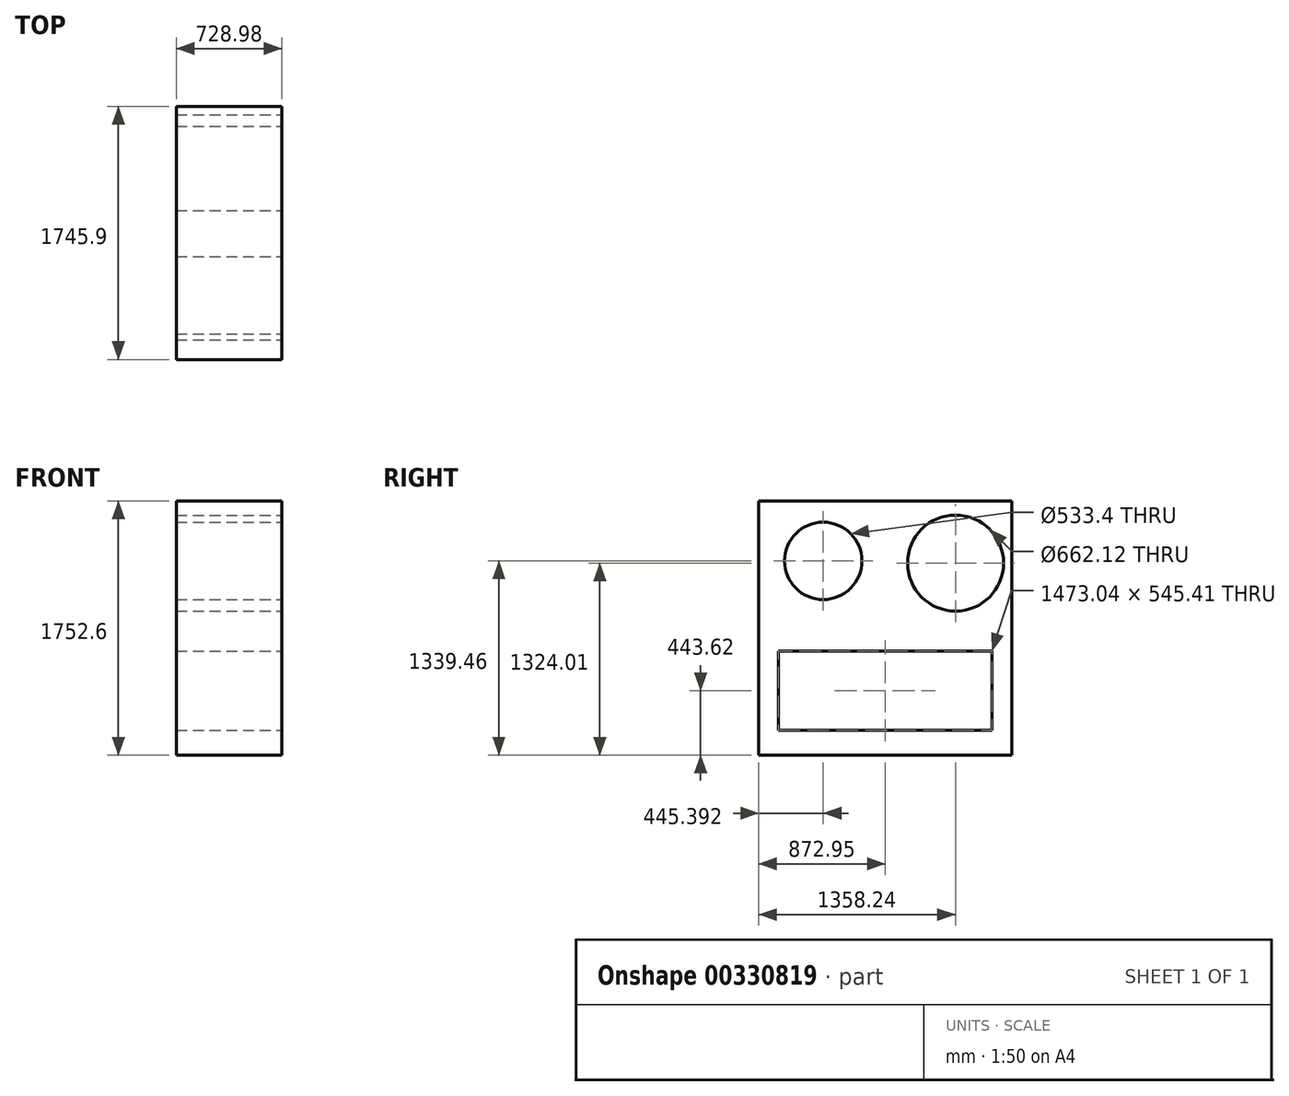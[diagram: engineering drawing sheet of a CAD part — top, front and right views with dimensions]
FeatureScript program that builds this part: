
annotation { "Feature Type Name" : "Feature", "Feature Type Description" : "" }
export const myFeature = defineFeature(function(context is Context, id is Id, definition is map)
    precondition{}
    {
        {
            var Q0;
            Q0=qCreatedBy(makeId("Right.planeOp"),FACE);
            var sketch = newSketch(context, id + "F0", { "sketchPlane" : qUnion([Q0])});
            skLineSegment(sketch, "E0.bottom", {"start": v(-872.95, -876.3) * mm, "end": v(872.95, -876.3) * mm});
            skLineSegment(sketch, "E0.top", {"start": v(-872.95, 876.3) * mm, "end": v(872.95, 876.3) * mm});
            skLineSegment(sketch, "E0.left", {"start": v(-872.95, -876.3) * mm, "end": v(-872.95, 876.3) * mm});
            skLineSegment(sketch, "E0.right", {"start": v(872.95, -876.3) * mm, "end": v(872.95, 876.3) * mm});
            skPoint(sketch, "E0.middle", {"position": v(0, 0) * mm});
            skSolve(sketch);
        }
        {
            var Q0;
            Q0 = qSketchRegion(id + "F0", true);
            extrude(context, id + "F1", {"entities" : qUnion([Q0]), "depth" : 728.98 * mm});
        }
        {
            var Q0;
            Q0=makeQuery(id+"F1.opExtrude","CAP_FACE",FACE,{"disambiguationData":[OSD([sQuery(id+"F0.wireOp",EDGE,"E0.bottom"),sQuery(id+"F0.wireOp",EDGE,"E0.top"),sQuery(id+"F0.wireOp",EDGE,"E0.left"),sQuery(id+"F0.wireOp",EDGE,"E0.right")])],"isStart":false});
            var sketch = newSketch(context, id + "F2", { "sketchPlane" : qUnion([Q0])});
            skCircle(sketch, "E1", {"center": v(-427.56, 463.16) * mm, "radius": 266.7 * mm});
            skSolve(sketch);
        }
        {
            var Q0;
            Q0=makeQuery(id+"F2.imprint","IMPRINT",FACE,{"disambiguationData":[TD([[makeQuery(id+"F2.imprint","IMPRINT",EDGE,{"derivedFrom":sQuery(id+"F2.wireOp",EDGE,"E1")}),1.0]])]});
            extrude(context, id + "F3", {"entities" : qUnion([Q0]), "operationType" : NewBodyOperationType.REMOVE, "oppositeDirection" : true, "depth" : 949.96 * mm});
        }
        {
            var Q0;
            Q0=makeQuery(id+"F1.opExtrude","CAP_FACE",FACE,{"disambiguationData":[OSD([sQuery(id+"F0.wireOp",EDGE,"E0.bottom"),sQuery(id+"F0.wireOp",EDGE,"E0.top"),sQuery(id+"F0.wireOp",EDGE,"E0.left"),sQuery(id+"F0.wireOp",EDGE,"E0.right")])],"isStart":false});
            var sketch = newSketch(context, id + "F4", { "sketchPlane" : qUnion([Q0])});
            skCircle(sketch, "E2", {"center": v(485.29, 447.71) * mm, "radius": 331.06 * mm});
            skLineSegment(sketch, "E3.bottom", {"start": v(736.52, -159.97) * mm, "end": v(-736.52, -159.97) * mm});
            skLineSegment(sketch, "E3.top", {"start": v(736.52, -705.39) * mm, "end": v(-736.52, -705.39) * mm});
            skLineSegment(sketch, "E3.left", {"start": v(736.52, -159.97) * mm, "end": v(736.52, -705.39) * mm});
            skLineSegment(sketch, "E3.right", {"start": v(-736.52, -159.97) * mm, "end": v(-736.52, -705.39) * mm});
            skPoint(sketch, "E3.middle", {"position": v(0, -432.68) * mm});
            skSolve(sketch);
        }
        {
            var Q0;
            Q0=makeQuery(id+"F4.imprint","IMPRINT",FACE,{"disambiguationData":[TD([[makeQuery(id+"F4.imprint","IMPRINT",EDGE,{"derivedFrom":sQuery(id+"F4.wireOp",EDGE,"E3.bottom")}),1.0]])]});
            var Q1;
            Q1=makeQuery(id+"F4.imprint","IMPRINT",FACE,{"disambiguationData":[TD([[makeQuery(id+"F4.imprint","IMPRINT",EDGE,{"derivedFrom":sQuery(id+"F4.wireOp",EDGE,"E2")}),1.0]])]});
            extrude(context, id + "F5", {"entities" : qUnion([Q0, Q1]), "operationType" : NewBodyOperationType.REMOVE, "oppositeDirection" : true, "depth" : 1889.76 * mm});
        }
    });
